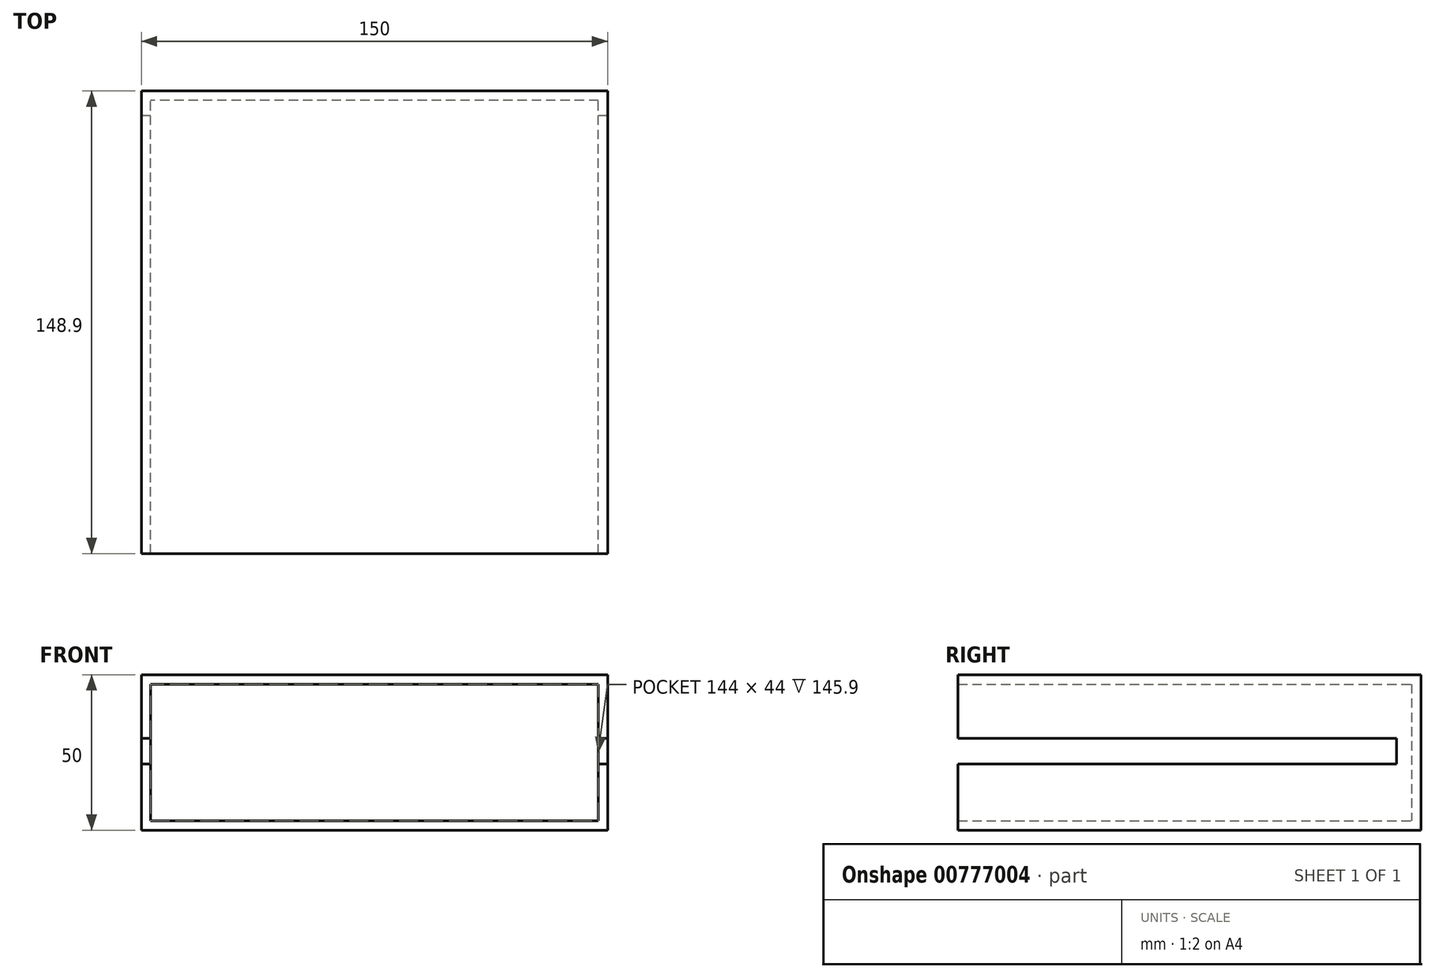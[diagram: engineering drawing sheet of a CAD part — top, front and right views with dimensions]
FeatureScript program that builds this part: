
annotation { "Feature Type Name" : "Feature", "Feature Type Description" : "" }
export const myFeature = defineFeature(function(context is Context, id is Id, definition is map)
    precondition{}
    {
        {
            var Q0;
            Q0=qCreatedBy(makeId("Front.planeOp"),FACE);
            var sketch = newSketch(context, id + "F0", { "sketchPlane" : qUnion([Q0])});
            skLineSegment(sketch, "E0.bottom", {"start": v(75, 25) * mm, "end": v(-75, 25) * mm});
            skLineSegment(sketch, "E0.top", {"start": v(75, -25) * mm, "end": v(-75, -25) * mm});
            skLineSegment(sketch, "E0.left", {"start": v(75, 25) * mm, "end": v(75, -25) * mm});
            skLineSegment(sketch, "E0.right", {"start": v(-75, 25) * mm, "end": v(-75, -25) * mm});
            skPoint(sketch, "E0.middle", {"position": v(0, 0) * mm});
            skSolve(sketch);
        }
        {
            var Q0;
            Q0=makeQuery(id+"F0.imprint","IMPRINT",FACE,{"disambiguationData":[TD([[makeQuery(id+"F0.imprint","IMPRINT",EDGE,{"derivedFrom":sQuery(id+"F0.wireOp",EDGE,"E0.bottom")}),1.0]])]});
            extrude(context, id + "F1", {"entities" : qUnion([Q0]), "depth" : 148.9 * mm, "offsetDistance" : 25 * mm});
        }
        {
            var Q0;
            Q0=makeQuery(id+"F1.opExtrude","CAP_FACE",FACE,{"disambiguationData":[OSD([sQuery(id+"F0.wireOp",EDGE,"E0.bottom"),sQuery(id+"F0.wireOp",EDGE,"E0.top"),sQuery(id+"F0.wireOp",EDGE,"E0.left"),sQuery(id+"F0.wireOp",EDGE,"E0.right")])],"isStart":false});
            shell(context, id + "F2", {"entities" : qUnion([Q0]), "thickness" : 3 * mm});
        }
        {
            var Q0;
            Q0=qCreatedBy(makeId("Right.planeOp"),FACE);
            var sketch = newSketch(context, id + "F3", { "sketchPlane" : qUnion([Q0])});
            skLineSegment(sketch, "E1.bottom", {"start": v(-7.9, -3.65) * mm, "end": v(-157, -3.65) * mm});
            skLineSegment(sketch, "E1.top", {"start": v(-7.9, 4.56) * mm, "end": v(-157, 4.56) * mm});
            skLineSegment(sketch, "E1.left", {"start": v(-7.9, -3.65) * mm, "end": v(-7.9, 4.56) * mm});
            skLineSegment(sketch, "E1.right", {"start": v(-157, -3.65) * mm, "end": v(-157, 4.56) * mm});
            skSolve(sketch);
        }
        {
            var Q0;
            Q0=qSketchRegion(id+"F3",true);
            extrude(context, id + "F4", {"entities" : qUnion([Q0]), "operationType" : NewBodyOperationType.REMOVE, "depth" : 98.5 * mm, "offsetDistance" : 25 * mm, "hasSecondDirection" : true, "secondDirectionOppositeDirection" : true, "secondDirectionDepth" : 98.4 * mm});
        }
    });
